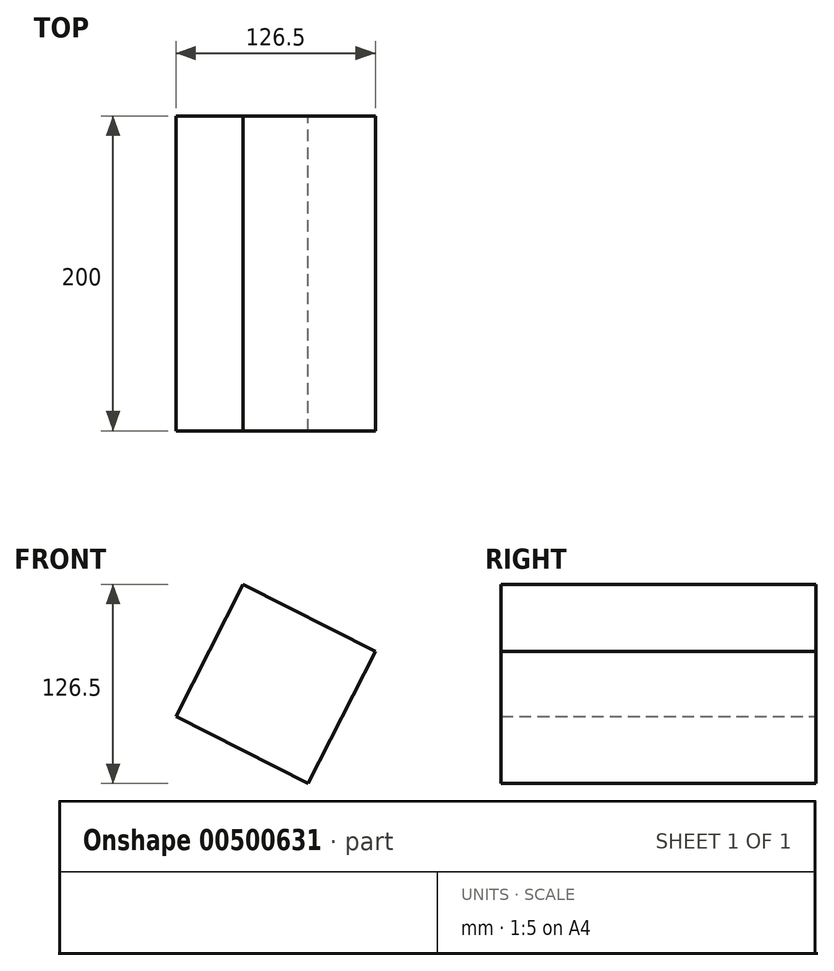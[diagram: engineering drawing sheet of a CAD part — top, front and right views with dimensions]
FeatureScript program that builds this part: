
annotation { "Feature Type Name" : "Feature", "Feature Type Description" : "" }
export const myFeature = defineFeature(function(context is Context, id is Id, definition is map)
    precondition{}
    {
        {
            var Q0;
            Q0=qCreatedBy(makeId("Front.planeOp"),FACE);
            var sketch = newSketch(context, id + "F0", { "sketchPlane" : qUnion([Q0])});
            skCircle(sketch, "E0.cCircle", {"center": v(0, -2.48) * mm, "radius": 47.06 * mm, "construction": true});
            skLineSegment(sketch, "E0.0", {"start": v(63.25, 18.22) * mm, "end": v(20.7, -65.73) * mm});
            skLineSegment(sketch, "E0.1", {"start": v(20.7, -65.73) * mm, "end": v(-63.25, -23.17) * mm});
            skLineSegment(sketch, "E0.2", {"start": v(-63.25, -23.17) * mm, "end": v(-20.7, 60.77) * mm});
            skLineSegment(sketch, "E0.3", {"start": v(-20.7, 60.77) * mm, "end": v(63.25, 18.22) * mm});
            skPoint(sketch, "E0.0.midPoint", {"position": v(41.97, -23.76) * mm});
            skSolve(sketch);
        }
        {
            var Q0;
            Q0=makeQuery(id+"F0.imprint","IMPRINT",FACE,{"disambiguationData":[TD([[makeQuery(id+"F0.imprint","IMPRINT",EDGE,{"derivedFrom":sQuery(id+"F0.wireOp",EDGE,"E0.0")}),-1.0]])]});
            extrude(context, id + "F1", {"entities" : qUnion([Q0]), "depth" : 200 * mm});
        }
    });
